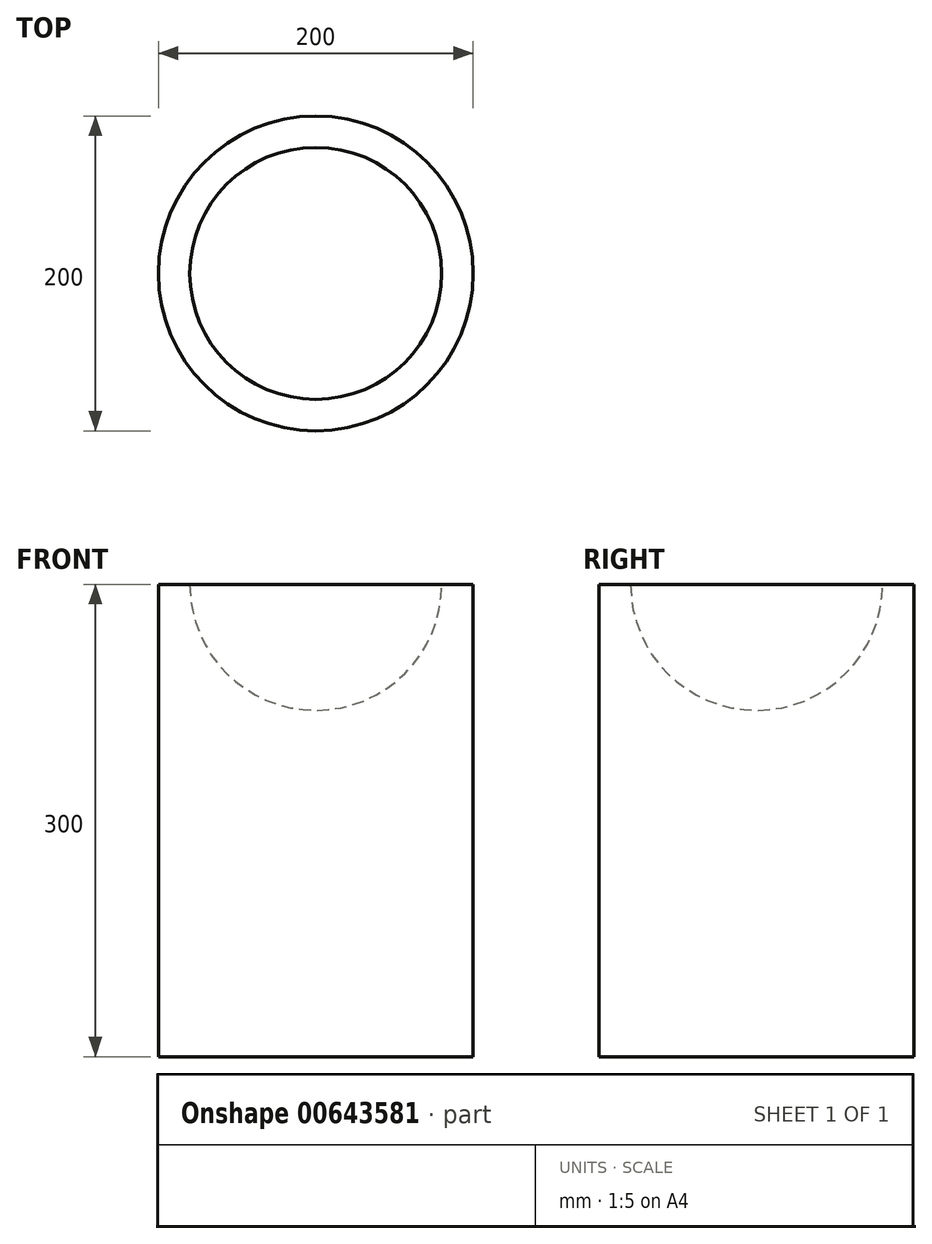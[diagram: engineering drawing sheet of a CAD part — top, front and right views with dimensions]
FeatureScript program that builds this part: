
annotation { "Feature Type Name" : "Feature", "Feature Type Description" : "" }
export const myFeature = defineFeature(function(context is Context, id is Id, definition is map)
    precondition{}
    {
        {
            var Q0;
            Q0=qCreatedBy(makeId("Top.planeOp"),FACE);
            var sketch = newSketch(context, id + "F0", { "sketchPlane" : qUnion([Q0])});
            skCircle(sketch, "E0", {"center": v(0, 0) * mm, "radius": 100 * mm});
            skSolve(sketch);
        }
        {
            var Q0;
            Q0=makeQuery(id+"F0.imprint","IMPRINT",FACE,{"disambiguationData":[TD([[makeQuery(id+"F0.imprint","IMPRINT",EDGE,{"derivedFrom":sQuery(id+"F0.wireOp",EDGE,"E0")}),1.0]])]});
            extrude(context, id + "F1", {"entities" : qUnion([Q0]), "depth" : 300 * mm, "offsetDistance" : 25 * mm});
        }
        {
            var Q0;
            Q0=makeQuery(id+"F1.opExtrude","CAP_FACE",FACE,{"disambiguationData":[OSD([sQuery(id+"F0.wireOp",EDGE,"E0")])],"isStart":false});
            var sketch = newSketch(context, id + "F2", { "sketchPlane" : qUnion([Q0])});
            skArc(sketch, "E1", {"start": v(0, 80) * mm, "mid": v(-80, 0) * mm, "end": v(0, -80) * mm});
            skLineSegment(sketch, "E2", {"start": v(0, 80) * mm, "end": v(0, -80) * mm});
            skSolve(sketch);
        }
        {
            var Q0;
            Q0 = qSketchRegion(id + "F2", true);
            var Q1;
            Q1=sQuery(id+"F2.wireOp",EDGE,"E2");
            revolve(context, id + "F3", {"operationType" : NewBodyOperationType.REMOVE, "entities" : qUnion([Q0]), "axis" : qUnion([Q1]), "revolveType" : RevolveType.FULL, "oppositeDirection" : true});
        }
    });
